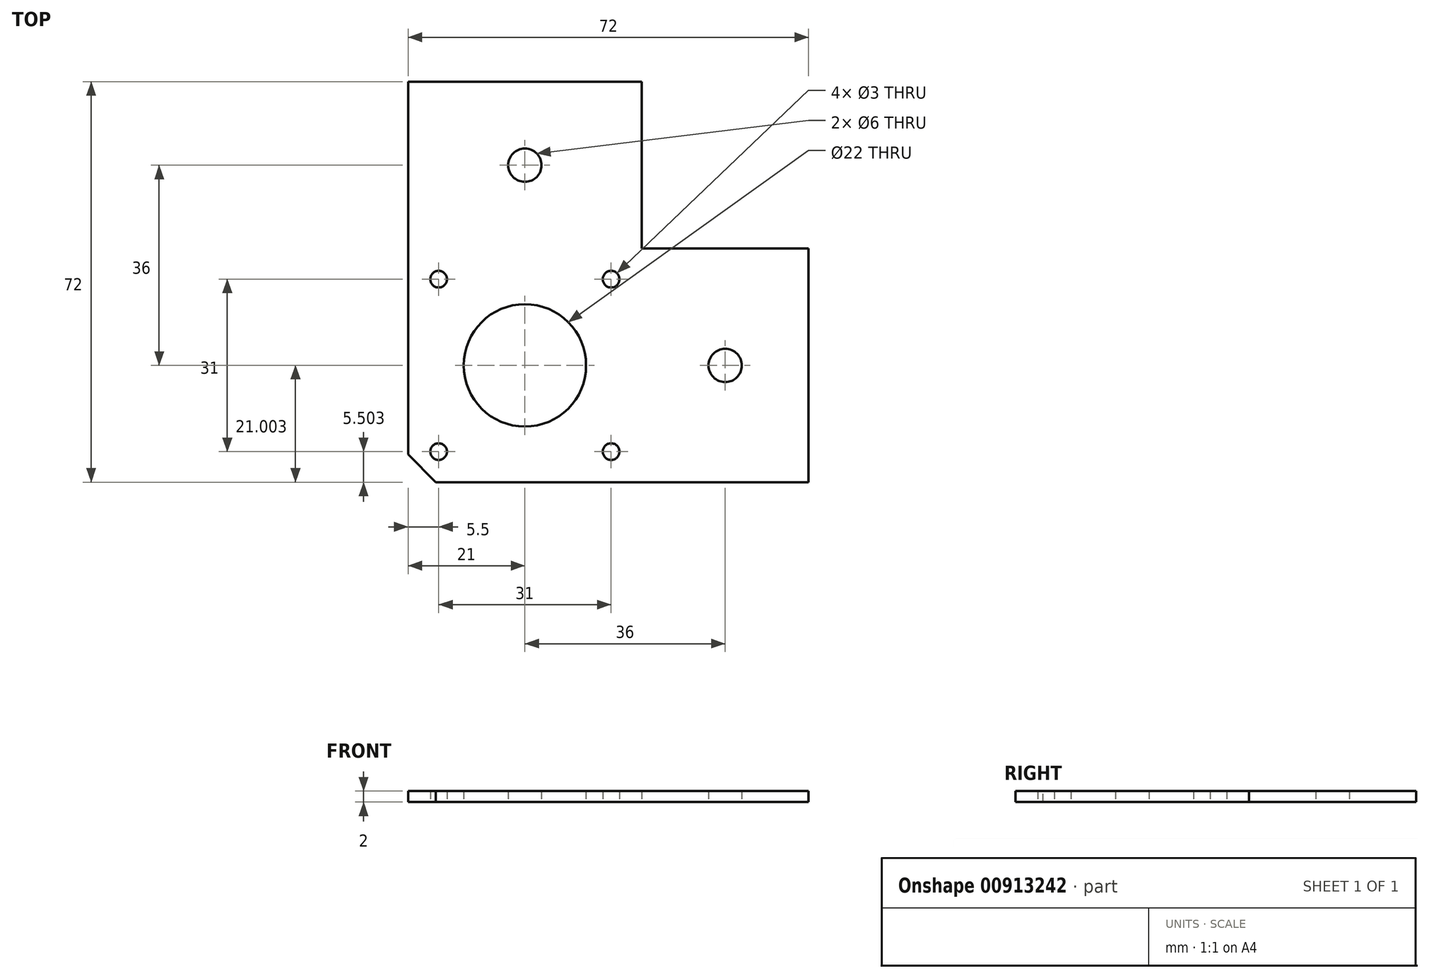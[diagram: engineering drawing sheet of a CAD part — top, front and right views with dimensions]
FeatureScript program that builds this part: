
annotation { "Feature Type Name" : "Feature", "Feature Type Description" : "" }
export const myFeature = defineFeature(function(context is Context, id is Id, definition is map)
    precondition{}
    {
        {
            var Q0;
            Q0=qCreatedBy(makeId("Top.planeOp"),FACE);
            var sketch = newSketch(context, id + "F0", { "sketchPlane" : qUnion([Q0])});
            skLineSegment(sketch, "E0.bottom", {"start": v(36, -37.67) * mm, "end": v(-36, -37.67) * mm});
            skLineSegment(sketch, "E0.top", {"start": v(36, 34.33) * mm, "end": v(-36, 34.33) * mm});
            skLineSegment(sketch, "E0.left", {"start": v(36, -37.67) * mm, "end": v(36, 34.33) * mm});
            skLineSegment(sketch, "E0.right", {"start": v(-36, -37.67) * mm, "end": v(-36, 34.33) * mm});
            skPoint(sketch, "E0.middle", {"position": v(0, -1.67) * mm});
            skLineSegment(sketch, "E1.bottom", {"start": v(36, 34.33) * mm, "end": v(6, 34.33) * mm});
            skLineSegment(sketch, "E1.top", {"start": v(36, 4.33) * mm, "end": v(6, 4.33) * mm});
            skLineSegment(sketch, "E1.left", {"start": v(36, 34.33) * mm, "end": v(36, 4.33) * mm});
            skLineSegment(sketch, "E1.right", {"start": v(6, 34.33) * mm, "end": v(6, 4.33) * mm});
            skCircle(sketch, "E2", {"center": v(-15, -16.67) * mm, "radius": 11 * mm});
            skCircle(sketch, "E3", {"center": v(-15, 19.33) * mm, "radius": 3 * mm});
            skCircle(sketch, "E4", {"center": v(21, -16.67) * mm, "radius": 3 * mm});
            skCircle(sketch, "E5", {"center": v(-30.5, -1.17) * mm, "radius": 1.5 * mm});
            skCircle(sketch, "E6", {"center": v(0.5, -1.17) * mm, "radius": 1.5 * mm});
            skCircle(sketch, "E7", {"center": v(0.5, -32.17) * mm, "radius": 1.5 * mm});
            skCircle(sketch, "E8", {"center": v(-30.5, -32.17) * mm, "radius": 1.5 * mm});
            skSolve(sketch);
        }
        {
            var Q0;
            Q0=makeQuery(id+"F0.imprint","IMPRINT",FACE,{"disambiguationData":[TD([[makeQuery(id+"F0.imprint","IMPRINT",EDGE,{"derivedFrom":sQuery(id+"F0.wireOp",EDGE,"E0.bottom")}),-1.0]])]});
            extrude(context, id + "F1", {"entities" : qUnion([Q0]), "depth" : 2 * mm, "offsetDistance" : 25 * mm});
        }
        {
            var Q0;
            Q0=makeQuery(id+"F1.opExtrude","SWEPT_EDGE",EDGE,{"disambiguationData":[OSD([sQuery(id+"F0.wireOp",EDGE,"E0.bottom"),sQuery(id+"F0.wireOp",EDGE,"E0.right")])]});
            chamfer(context, id + "F2", {"entities" : qUnion([Q0]), "width" : 5 * mm, "tangentPropagation" : true});
        }
    });
